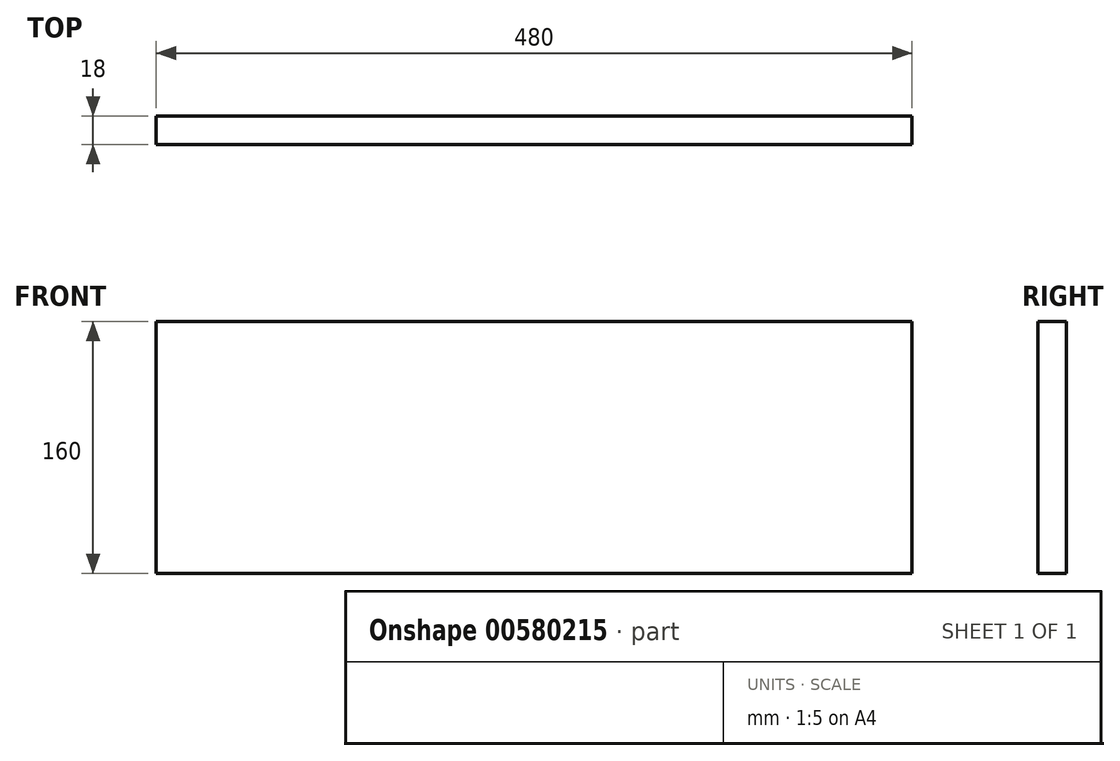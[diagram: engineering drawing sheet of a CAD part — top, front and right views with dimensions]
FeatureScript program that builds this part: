
annotation { "Feature Type Name" : "Feature", "Feature Type Description" : "" }
export const myFeature = defineFeature(function(context is Context, id is Id, definition is map)
    precondition{}
    {
        {
            var Q0;
            Q0=qCreatedBy(makeId("Front.planeOp"),FACE);
            var sketch = newSketch(context, id + "F0", { "sketchPlane" : qUnion([Q0])});
            skLineSegment(sketch, "E0.bottom", {"start": v(240, 80) * mm, "end": v(-240, 80) * mm});
            skLineSegment(sketch, "E0.top", {"start": v(240, -80) * mm, "end": v(-240, -80) * mm});
            skLineSegment(sketch, "E0.left", {"start": v(240, 80) * mm, "end": v(240, -80) * mm});
            skLineSegment(sketch, "E0.right", {"start": v(-240, 80) * mm, "end": v(-240, -80) * mm});
            skPoint(sketch, "E0.middle", {"position": v(0, 0) * mm});
            skSolve(sketch);
        }
        {
            var Q0;
            Q0=makeQuery(id+"F0.imprint","IMPRINT",FACE,{"disambiguationData":[TD([[makeQuery(id+"F0.imprint","IMPRINT",EDGE,{"derivedFrom":sQuery(id+"F0.wireOp",EDGE,"E0.bottom")}),1.0]])]});
            extrude(context, id + "F1", {"entities" : qUnion([Q0]), "oppositeDirection" : true, "depth" : 18 * mm, "offsetDistance" : 25 * mm});
        }
    });
